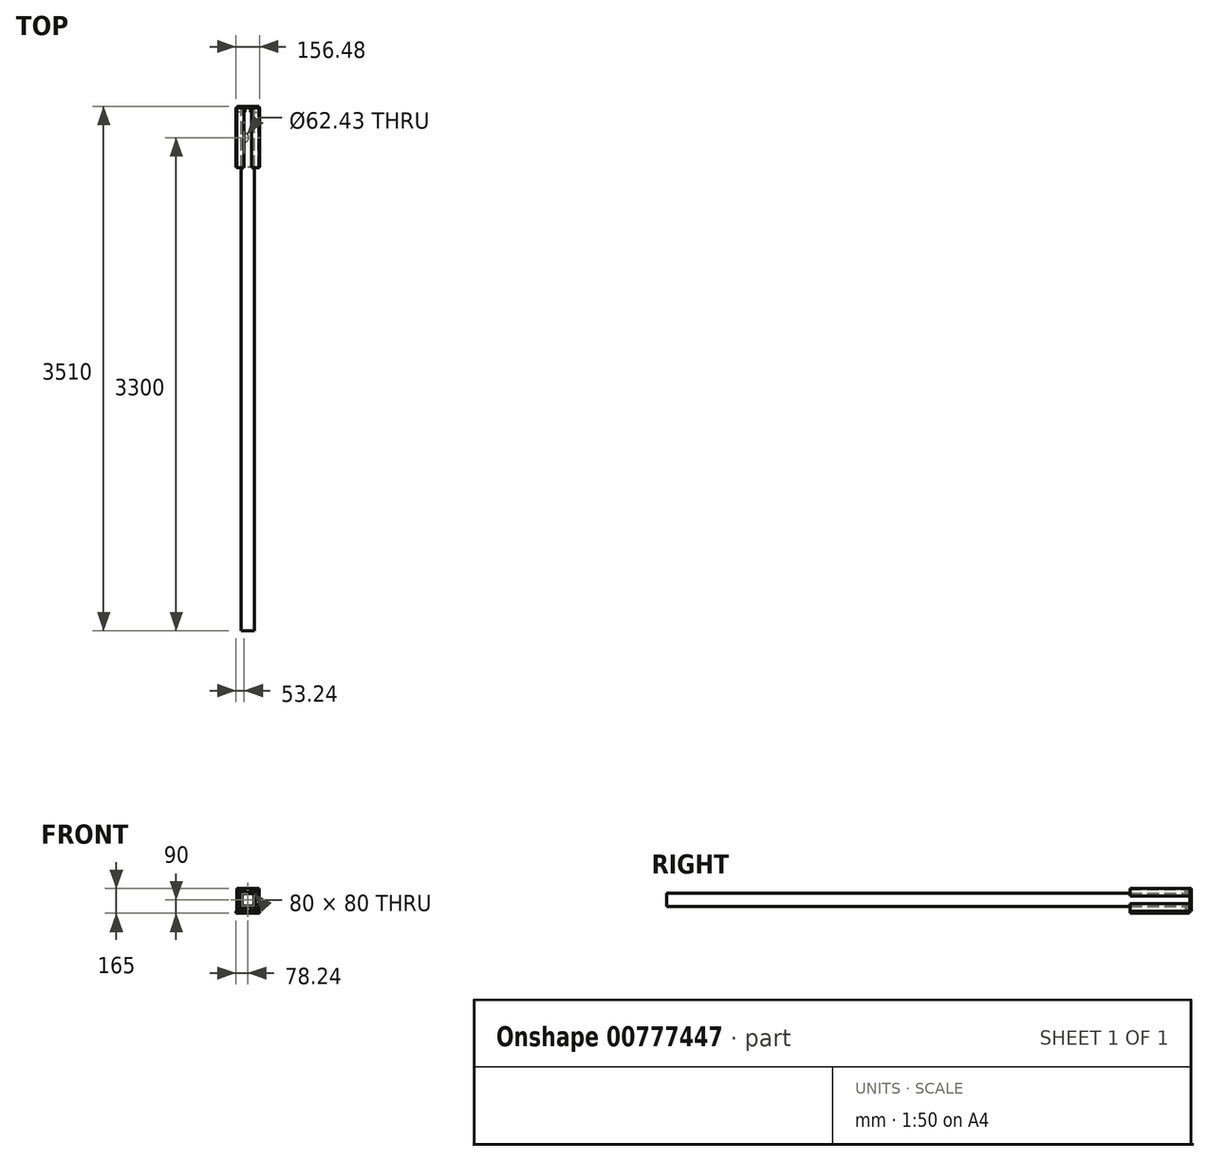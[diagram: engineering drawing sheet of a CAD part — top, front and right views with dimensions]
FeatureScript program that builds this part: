
annotation { "Feature Type Name" : "Feature", "Feature Type Description" : "" }
export const myFeature = defineFeature(function(context is Context, id is Id, definition is map)
    precondition{}
    {
        {
            var Q0;
            Q0=qCreatedBy(makeId("Front.planeOp"),FACE);
            var sketch = newSketch(context, id + "F0", { "sketchPlane" : qUnion([Q0])});
            skLineSegment(sketch, "E0.bottom", {"start": v(40, 40) * mm, "end": v(-40, 40) * mm});
            skLineSegment(sketch, "E0.top", {"start": v(40, -40) * mm, "end": v(-40, -40) * mm});
            skLineSegment(sketch, "E0.left", {"start": v(40, 40) * mm, "end": v(40, -40) * mm});
            skLineSegment(sketch, "E0.right", {"start": v(-40, 40) * mm, "end": v(-40, -40) * mm});
            skPoint(sketch, "E0.middle", {"position": v(0, 0) * mm});
            skLineSegment(sketch, "E1.0", {"start": v(45, -45) * mm, "end": v(-45, -45) * mm});
            skLineSegment(sketch, "E1.1", {"start": v(45, 45) * mm, "end": v(45, -45) * mm});
            skLineSegment(sketch, "E1.2", {"start": v(45, 45) * mm, "end": v(-45, 45) * mm});
            skLineSegment(sketch, "E1.3", {"start": v(-45, 45) * mm, "end": v(-45, -45) * mm});
            skLineSegment(sketch, "E2", {"start": v(-25, -70) * mm, "end": v(-70, -70) * mm});
            skLineSegment(sketch, "E3", {"start": v(-70, -70) * mm, "end": v(-70, -25) * mm});
            skLineSegment(sketch, "E4", {"start": v(-70, -25) * mm, "end": v(-75, -25) * mm});
            skLineSegment(sketch, "E5", {"start": v(-75, -25) * mm, "end": v(-75, -75) * mm});
            skLineSegment(sketch, "E6", {"start": v(-75, -75) * mm, "end": v(-25, -75) * mm});
            skLineSegment(sketch, "E7", {"start": v(-25, -75) * mm, "end": v(-25, -70) * mm});
            skLineSegment(sketch, "E8.bottom", {"start": v(-45, -32.2) * mm, "end": v(-69, -32.2) * mm});
            skLineSegment(sketch, "E8.top", {"start": v(-45, -57.2) * mm, "end": v(-69, -57.2) * mm});
            skLineSegment(sketch, "E8.left", {"start": v(-45, -32.2) * mm, "end": v(-45, -57.2) * mm});
            skLineSegment(sketch, "E8.right", {"start": v(-69, -32.2) * mm, "end": v(-69, -57.2) * mm});
            skPoint(sketch, "E8.middle", {"position": v(-57, -44.7) * mm});
            skLineSegment(sketch, "E9.bottom", {"start": v(-17.9, -45) * mm, "end": v(-42.9, -45) * mm});
            skLineSegment(sketch, "E9.top", {"start": v(-17.9, -69) * mm, "end": v(-42.9, -69) * mm});
            skLineSegment(sketch, "E9.left", {"start": v(-17.9, -45) * mm, "end": v(-17.9, -69) * mm});
            skLineSegment(sketch, "E9.right", {"start": v(-42.9, -45) * mm, "end": v(-42.9, -69) * mm});
            skPoint(sketch, "E9.middle", {"position": v(-30.4, -57) * mm});
            skLineSegment(sketch, "E10.MirrorCS", {"start": v(25, -75) * mm, "end": v(25, -70) * mm});
            skLineSegment(sketch, "E11.MirrorCS", {"start": v(25, -70) * mm, "end": v(70, -70) * mm});
            skLineSegment(sketch, "E12.MirrorCS", {"start": v(17.9, -45) * mm, "end": v(42.9, -45) * mm});
            skLineSegment(sketch, "E13.MirrorCS", {"start": v(17.9, -69) * mm, "end": v(42.9, -69) * mm});
            skLineSegment(sketch, "E14.MirrorCS", {"start": v(17.9, -45) * mm, "end": v(17.9, -69) * mm});
            skLineSegment(sketch, "E15.MirrorCS", {"start": v(42.9, -45) * mm, "end": v(42.9, -69) * mm});
            skLineSegment(sketch, "E16.MirrorCS", {"start": v(45, -32.2) * mm, "end": v(45, -57.2) * mm});
            skLineSegment(sketch, "E17.MirrorCS", {"start": v(45, -57.2) * mm, "end": v(69, -57.2) * mm});
            skLineSegment(sketch, "E18.MirrorCS", {"start": v(45, -32.2) * mm, "end": v(69, -32.2) * mm});
            skLineSegment(sketch, "E19.MirrorCS", {"start": v(69, -32.2) * mm, "end": v(69, -57.2) * mm});
            skLineSegment(sketch, "E20.MirrorCS", {"start": v(70, -70) * mm, "end": v(70, -25) * mm});
            skLineSegment(sketch, "E21.MirrorCS", {"start": v(70, -25) * mm, "end": v(75, -25) * mm});
            skLineSegment(sketch, "E22.MirrorCS", {"start": v(75, -75) * mm, "end": v(25, -75) * mm});
            skLineSegment(sketch, "E23.MirrorCS", {"start": v(75, -25) * mm, "end": v(75, -75) * mm});
            skLineSegment(sketch, "E24.MirrorCS", {"start": v(25, 75) * mm, "end": v(25, 70) * mm});
            skLineSegment(sketch, "E25.MirrorCS", {"start": v(70, 25) * mm, "end": v(75, 25) * mm});
            skLineSegment(sketch, "E26.MirrorCS", {"start": v(-42.9, 45) * mm, "end": v(-42.9, 69) * mm});
            skLineSegment(sketch, "E27.MirrorCS", {"start": v(45, 32.2) * mm, "end": v(45, 57.2) * mm});
            skLineSegment(sketch, "E28.MirrorCS", {"start": v(-25, 75) * mm, "end": v(-25, 70) * mm});
            skLineSegment(sketch, "E29.MirrorCS", {"start": v(-45, 32.2) * mm, "end": v(-45, 57.2) * mm});
            skLineSegment(sketch, "E30.MirrorCS", {"start": v(42.9, 45) * mm, "end": v(42.9, 69) * mm});
            skLineSegment(sketch, "E31.MirrorCS", {"start": v(-70, 25) * mm, "end": v(-75, 25) * mm});
            skLineSegment(sketch, "E32.MirrorCS", {"start": v(-45, 32.2) * mm, "end": v(-69, 32.2) * mm});
            skLineSegment(sketch, "E33.MirrorCS", {"start": v(-17.9, 69) * mm, "end": v(-42.9, 69) * mm});
            skLineSegment(sketch, "E34.MirrorCS", {"start": v(-17.9, 45) * mm, "end": v(-17.9, 69) * mm});
            skLineSegment(sketch, "E35.MirrorCS", {"start": v(75, 75) * mm, "end": v(25, 75) * mm});
            skPoint(sketch, "E36.MirrorP", {"position": v(-57, 44.7) * mm});
            skLineSegment(sketch, "E37.MirrorCS", {"start": v(-17.9, 45) * mm, "end": v(-42.9, 45) * mm});
            skLineSegment(sketch, "E38.MirrorCS", {"start": v(69, 32.2) * mm, "end": v(69, 57.2) * mm});
            skLineSegment(sketch, "E39.MirrorCS", {"start": v(17.9, 69) * mm, "end": v(42.9, 69) * mm});
            skLineSegment(sketch, "E40.MirrorCS", {"start": v(-69, 32.2) * mm, "end": v(-69, 57.2) * mm});
            skLineSegment(sketch, "E41.MirrorCS", {"start": v(45, 32.2) * mm, "end": v(69, 32.2) * mm});
            skLineSegment(sketch, "E42.MirrorCS", {"start": v(17.9, 45) * mm, "end": v(42.9, 45) * mm});
            skLineSegment(sketch, "E43.MirrorCS", {"start": v(70, 70) * mm, "end": v(70, 25) * mm});
            skLineSegment(sketch, "E44.MirrorCS", {"start": v(-45, 57.2) * mm, "end": v(-69, 57.2) * mm});
            skLineSegment(sketch, "E45.MirrorCS", {"start": v(75, 25) * mm, "end": v(75, 75) * mm});
            skPoint(sketch, "E46.MirrorP", {"position": v(-30.4, 57) * mm});
            skLineSegment(sketch, "E47.MirrorCS", {"start": v(25, 70) * mm, "end": v(70, 70) * mm});
            skLineSegment(sketch, "E48.MirrorCS", {"start": v(-75, 75) * mm, "end": v(-25, 75) * mm});
            skLineSegment(sketch, "E49.MirrorCS", {"start": v(17.9, 45) * mm, "end": v(17.9, 69) * mm});
            skLineSegment(sketch, "E50.MirrorCS", {"start": v(-70, 70) * mm, "end": v(-70, 25) * mm});
            skLineSegment(sketch, "E51.MirrorCS", {"start": v(45, 57.2) * mm, "end": v(69, 57.2) * mm});
            skLineSegment(sketch, "E52.MirrorCS", {"start": v(-25, 70) * mm, "end": v(-70, 70) * mm});
            skLineSegment(sketch, "E53.MirrorCS", {"start": v(-75, 25) * mm, "end": v(-75, 75) * mm});
            skSolve(sketch);
        }
        {
            var Q0;
            Q0=makeQuery(id+"F0.imprint","IMPRINT",FACE,{"disambiguationData":[TD([[makeQuery(id+"F0.imprint","IMPRINT",EDGE,{"derivedFrom":sQuery(id+"F0.wireOp",EDGE,"E0.bottom")}),-1.0]])]});
            extrude(context, id + "F1", {"entities" : qUnion([Q0]), "depth" : 3500 * mm, "offsetDistance" : 25 * mm});
        }
        {
            var Q0;
            Q0=makeQuery(id+"F0.imprint","IMPRINT",FACE,{"disambiguationData":[TD([[makeQuery(id+"F0.imprint","IMPRINT",EDGE,{"derivedFrom":sQuery(id+"F0.wireOp",EDGE,"E2")}),1.0]])]});
            var Q1;
            Q1=makeQuery(id+"F0.imprint","IMPRINT",FACE,{"disambiguationData":[TD([[makeQuery(id+"F0.imprint","IMPRINT",EDGE,{"derivedFrom":sQuery(id+"F0.wireOp",EDGE,"E10.MirrorCS")}),-1.0]])]});
            var Q2;
            Q2=makeQuery(id+"F0.imprint","IMPRINT",FACE,{"disambiguationData":[TD([[makeQuery(id+"F0.imprint","IMPRINT",EDGE,{"derivedFrom":sQuery(id+"F0.wireOp",EDGE,"E24.MirrorCS")}),1.0]])]});
            var Q3;
            Q3=makeQuery(id+"F0.imprint","IMPRINT",FACE,{"disambiguationData":[TD([[makeQuery(id+"F0.imprint","IMPRINT",EDGE,{"derivedFrom":sQuery(id+"F0.wireOp",EDGE,"E28.MirrorCS")}),-1.0]])]});
            extrude(context, id + "F2", {"entities" : qUnion([Q0, Q1, Q2, Q3]), "depth" : 400 * mm, "offsetDistance" : 25 * mm});
        }
        {
            var Q0;
            {var subQ1=sQuery(id+"F0.wireOp",EDGE,"E8.bottom");Q0=makeQuery(id+"F0.imprint","IMPRINT",FACE,{"disambiguationData":[TD([[makeQuery(id+"F0.imprint","IMPRINT",EDGE,{"derivedFrom":subQ1}),1.0]])]});}
            var Q1;
            {var subQ0=sQuery(id+"F0.wireOp",EDGE,"E16.MirrorCS");Q1=makeQuery(id+"F0.imprint","IMPRINT",FACE,{"disambiguationData":[TD([[makeQuery(id+"F0.imprint","IMPRINT",EDGE,{"derivedFrom":subQ0}),1.0]])]});}
            var Q2;
            {var subQ0=sQuery(id+"F0.wireOp",EDGE,"E27.MirrorCS");Q2=makeQuery(id+"F0.imprint","IMPRINT",FACE,{"disambiguationData":[TD([[makeQuery(id+"F0.imprint","IMPRINT",EDGE,{"derivedFrom":subQ0}),-1.0]])]});}
            var Q3;
            {var subQ1=sQuery(id+"F0.wireOp",EDGE,"E29.MirrorCS");Q3=makeQuery(id+"F0.imprint","IMPRINT",FACE,{"disambiguationData":[TD([[makeQuery(id+"F0.imprint","IMPRINT",EDGE,{"derivedFrom":subQ1}),1.0]])]});}
            extrude(context, id + "F3", {"entities" : qUnion([Q0, Q1, Q2, Q3]), "operationType" : NewBodyOperationType.ADD, "depth" : 30 * mm, "offsetDistance" : 25 * mm});
        }
        {
            var Q0;
            Q0=makeQuery(id+"F0.imprint","IMPRINT",FACE,{"disambiguationData":[TD([[makeQuery(id+"F0.imprint","IMPRINT",EDGE,{"derivedFrom":sQuery(id+"F0.wireOp",EDGE,"E9.top")}),-1.0]])]});
            var Q1;
            Q1=makeQuery(id+"F0.imprint","IMPRINT",FACE,{"disambiguationData":[TD([[makeQuery(id+"F0.imprint","IMPRINT",EDGE,{"derivedFrom":sQuery(id+"F0.wireOp",EDGE,"E13.MirrorCS")}),1.0]])]});
            var Q2;
            {var subQ2=sQuery(id+"F0.wireOp",EDGE,"E30.MirrorCS");Q2=makeQuery(id+"F0.imprint","IMPRINT",FACE,{"disambiguationData":[TD([[makeQuery(id+"F0.imprint","IMPRINT",EDGE,{"derivedFrom":subQ2}),1.0]])]});}
            var Q3;
            {var subQ0=sQuery(id+"F0.wireOp",EDGE,"E26.MirrorCS");Q3=makeQuery(id+"F0.imprint","IMPRINT",FACE,{"disambiguationData":[TD([[makeQuery(id+"F0.imprint","IMPRINT",EDGE,{"derivedFrom":subQ0}),-1.0]])]});}
            extrude(context, id + "F4", {"entities" : qUnion([Q0, Q1, Q2, Q3]), "operationType" : NewBodyOperationType.ADD, "depth" : 30 * mm, "offsetDistance" : 25 * mm});
        }
        {
            var Q0;
            Q0=makeQuery(id+"F0.imprint","IMPRINT",FACE,{"disambiguationData":[TD([[makeQuery(id+"F0.imprint","IMPRINT",EDGE,{"derivedFrom":sQuery(id+"F0.wireOp",EDGE,"E0.bottom")}),1.0]])]});
            var sketch = newSketch(context, id + "F5", { "sketchPlane" : qUnion([Q0])});
            skLineSegment(sketch, "E54.bottom", {"start": v(75, 75) * mm, "end": v(-75, 75) * mm});
            skLineSegment(sketch, "E54.top", {"start": v(75, -75) * mm, "end": v(17.27, -75) * mm});
            skLineSegment(sketch, "E54.left", {"start": v(75, 75) * mm, "end": v(75, -75) * mm});
            skLineSegment(sketch, "E54.right", {"start": v(-75, 75) * mm, "end": v(-75, -75) * mm});
            skPoint(sketch, "E54.middle", {"position": v(0, 0) * mm});
            skLineSegment(sketch, "E55.bottom", {"start": v(50, -50) * mm, "end": v(-50, -50) * mm});
            skLineSegment(sketch, "E55.top", {"start": v(50, 50) * mm, "end": v(-50, 50) * mm});
            skLineSegment(sketch, "E55.left", {"start": v(50, -50) * mm, "end": v(50, 50) * mm});
            skLineSegment(sketch, "E55.right", {"start": v(-50, -50) * mm, "end": v(-50, 50) * mm});
            skLineSegment(sketch, "E56", {"start": v(-16.43, -50) * mm, "end": v(-16.43, -75) * mm});
            skLineSegment(sketch, "E57", {"start": v(17.27, -50) * mm, "end": v(17.27, -75) * mm});
            skLineSegment(sketch, "E58.trimOffspring", {"start": v(-16.43, -75) * mm, "end": v(-75, -75) * mm});
            skSolve(sketch);
        }
        {
            var Q0;
            Q0=makeQuery(id+"F5.imprint","IMPRINT",FACE,{"disambiguationData":[TD([[makeQuery(id+"F5.imprint","IMPRINT",EDGE,{"derivedFrom":sQuery(id+"F5.wireOp",EDGE,"E54.bottom")}),1.0]])]});
            extrude(context, id + "F6", {"entities" : qUnion([Q0]), "oppositeDirection" : true, "depth" : 10 * mm, "offsetDistance" : 25 * mm});
        }
        {
            var Q0;
            Q0=makeQuery(id+"F2.opExtrude","SWEPT_FACE",FACE,{"disambiguationData":[OSD([sQuery(id+"F0.wireOp",EDGE,"E6")])]});
            var sketch = newSketch(context, id + "F7", { "sketchPlane" : qUnion([Q0])});
            skLineSegment(sketch, "E59.bottom", {"start": v(78.24, 398.37) * mm, "end": v(-78.24, 398.37) * mm});
            skLineSegment(sketch, "E59.top", {"start": v(78.24, 1.63) * mm, "end": v(-78.24, 1.63) * mm});
            skLineSegment(sketch, "E59.left", {"start": v(78.24, 398.37) * mm, "end": v(78.24, 1.63) * mm});
            skLineSegment(sketch, "E59.right", {"start": v(-78.24, 398.37) * mm, "end": v(-78.24, 1.63) * mm});
            skPoint(sketch, "E59.middle", {"position": v(0, 200) * mm});
            skPoint(sketch, "E59.middle.positionSnap0", {"position": v(-25, 200) * mm});
            skPoint(sketch, "E59.centerSnap0", {"position": v(-25, 200) * mm});
            skCircle(sketch, "E60", {"center": v(-25, 200) * mm, "radius": 31.22 * mm});
            skSolve(sketch);
        }
        {
            var Q0;
            Q0 = qSketchRegion(id + "F7", true);
            extrude(context, id + "F8", {"entities" : qUnion([Q0]), "depth" : 15 * mm, "offsetDistance" : 25 * mm});
        }
        {
            var Q0;
            Q0=makeQuery(id+"F2.opExtrude","SWEPT_FACE",FACE,{"disambiguationData":[OSD([sQuery(id+"F0.wireOp",EDGE,"E6")])]});
            extrude(context, id + "F9", {"entities" : qUnion([Q0]), "endBound" : BoundingType.UP_TO_NEXT, "oppositeDirection" : true, "depth" : 25 * mm, "offsetDistance" : 25 * mm});
        }
    });
